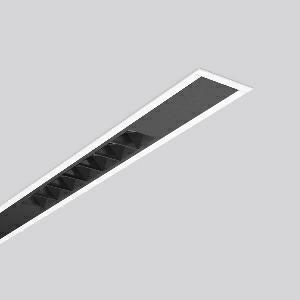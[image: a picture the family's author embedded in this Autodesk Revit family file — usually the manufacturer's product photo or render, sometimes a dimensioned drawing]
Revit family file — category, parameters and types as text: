
# Revit family: less_is_more_beamline_312472_002_76_7de1
name_source: partatom
category: Lighting Fixtures
units: mm (PartAtom-declared; Revit-internal decimal feet)

## family parameters
Cut with Voids When Loaded = No
Host = Face
Light Source = No
Part Type = Normal
Room Calculation Point = No
Round Connector Dimension = Use Diameter
Shared = No

## types (1)
- LESS IS MORE BEAMLINE (1 x LED Modul 930, 966.67 lm, 3000)
    Apparent Load = 35 VA
    CIE Flux Codes = 100 100 100 100 100
    Color Rendering = 90
    Color Temperature = 3000
    Default Elevation = 1800 mm
    Description = Series: LESS IS MORE BEAMLINE
Linear recessed ceiling and wall luminaire for aesthetically sophisticated lighting. Luminaire with three LED light units. Housing: extruded aluminium profile, powder-coated. End cap aluminium powder-coated. LED light unit with MRS technology: Mini-Reflector-System made of metallised thermoplastic with prismatic black glare-suppressing frame for pleasant glare-free light (RUG < 10). Each LED light unit has 7 reflector elements. Medium beam light distribution. Ceiling installation with pre-assembled SBS mounting system. LED unit with integrated converter interchangeable and removable. Suitable for through-wiring. 
Colour: traffic white, matt (RAL 9016)
Length: 1702 mm
Width: 71 mm
Height: 1.5 mm
Cut-out length: 1688 mm
Cut-out width: 60 mm
Recess height: 125 mm
Luminaire: recess height: 106 mm
Lamp: LED
Socket: without socket
Colour temperature: 3000K
Colour rendering index (CRI): 90
System power: 35 W
Rated luminous flux: 2900 lm
Luminous efficiency: 83 lm/W
Control gear: Converter, dimmable, DALI
Protection class: I
Type of protection: IP 20
    Height = 0 mm  [stored 0 ft]
    Lamp = 1 x LED Modul 930
    Lamp Light Flux = 966.67 lm
    Lamp count = 1
    Length = 1702 mm
    Lifetime = 50000 h
    Luminous efficacy = 83 lm/W
    Manufacturer = RZB
    ModVariant = No
    Model = 312472.002.76
    Mounting Place = Ceiling, Wall
    Mounting Type = Recessed
    Number of Poles = 1
    OnlyDefault = Yes
    Power Factor = 1
    Product Name = LESS IS MORE BEAMLINE
    Product group = Recessed LED linear luminaires
    ProductGroupID = 407
    Protection Class = Protection class I
    Protection Degree = IP 20
    RLX_Detail_Level = 1
    RLX_Emergency_Light_Flux = 0 lm
    RLX_Emergency_Type = 0
    RLX_Emergency_Type_DB = No
    RlxData = <blob elided: 23937 chars, md5=e77f3cf7>
    Socket = socket
    Standby Power = 0 W
    System Light Flux = 2900 lm
    System Power = 35 W
    Type Comments = Product without accessories
    Type Image = 312465.002.jpg
    URL = http://relux.com
    VarID = ---
    Voltage = 230 V
    Voltage Range = 220-240 V
    Weight = 0.00 kg
    Width = 71 mm

note: [stored X ft] marks values corroborated as IEEE doubles in the binary element streams (Revit-internal decimal feet)

## geometry (parser evidence)
native form markers: Blend x4, Sweep x17
no freeform markers — native parametric forms only
